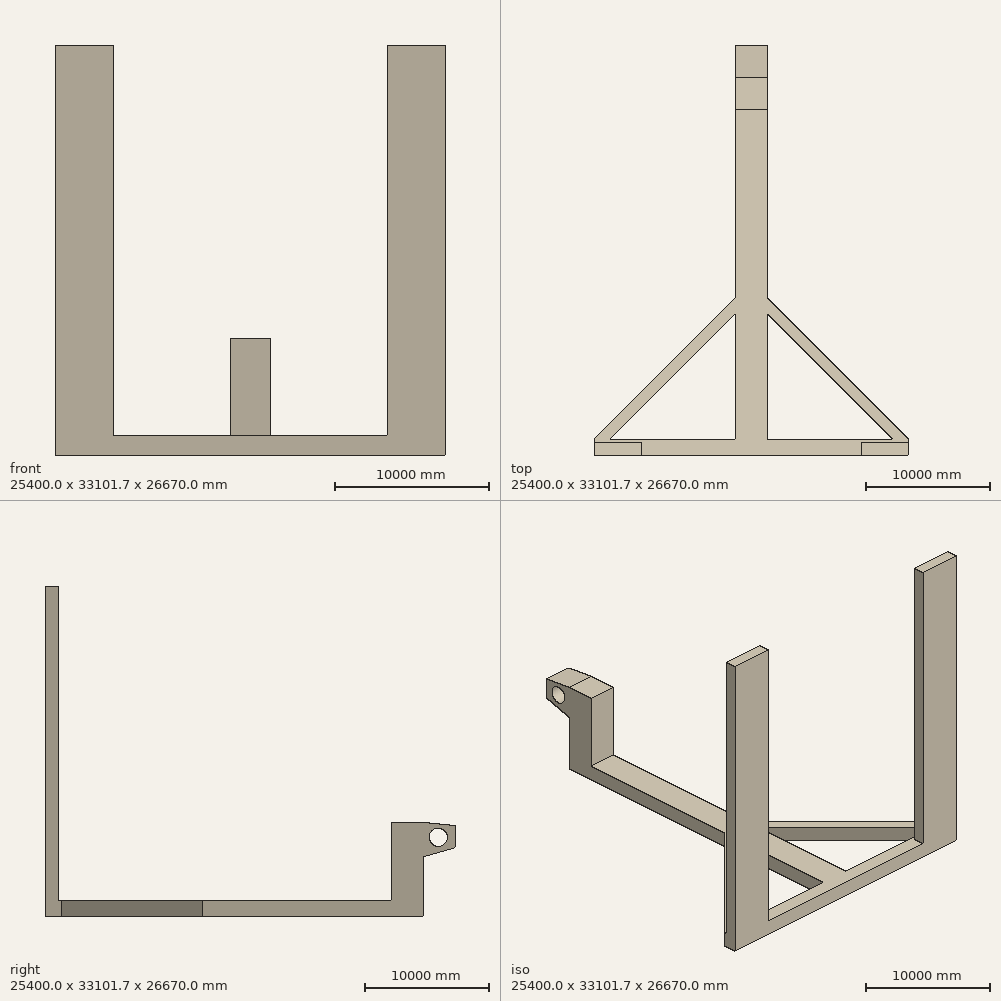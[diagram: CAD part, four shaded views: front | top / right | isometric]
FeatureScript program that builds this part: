
annotation { "Feature Type Name" : "Feature", "Feature Type Description" : "" }
export const myFeature = defineFeature(function(context is Context, id is Id, definition is map)
    precondition{}
    {
        {
            var Q0;
            Q0=qCreatedBy(makeId("Top.planeOp"),FACE);
            var sketch = newSketch(context, id + "F0", { "sketchPlane" : qUnion([Q0])});
            skLineSegment(sketch, "E0", {"start": v(0, 0) * mm, "end": v(28579.32, 0) * mm, "construction": true});
            skLineSegment(sketch, "E1", {"start": v(0, 0) * mm, "end": v(0, 20717.35) * mm, "construction": true});
            skLineSegment(sketch, "E2", {"start": v(0, 0) * mm, "end": v(0, 30480) * mm});
            skLineSegment(sketch, "E3", {"start": v(0, 30480) * mm, "end": v(1270, 30480) * mm});
            skLineSegment(sketch, "E4", {"start": v(1270, 30480) * mm, "end": v(1270, 12700) * mm});
            skLineSegment(sketch, "E5", {"start": v(1270, 12700) * mm, "end": v(12700, 1270) * mm});
            skLineSegment(sketch, "E6", {"start": v(12700, 1270) * mm, "end": v(12700, 0) * mm});
            skLineSegment(sketch, "E7", {"start": v(12700, 0) * mm, "end": v(0, 0) * mm});
            skLineSegment(sketch, "E8", {"start": v(1270, 11430) * mm, "end": v(1270, 1270) * mm});
            skLineSegment(sketch, "E9", {"start": v(1270, 1270) * mm, "end": v(11430, 1270) * mm});
            skLineSegment(sketch, "E10", {"start": v(11430, 1270) * mm, "end": v(1270, 11430) * mm});
            skSolve(sketch);
        }
        {
            var Q0;
            Q0 = qSketchRegion(id + "F0", true);
            extrude(context, id + "F1", {"entities" : qUnion([Q0]), "depth" : 1270 * mm, "offsetDistance" : 25.4 * mm});
        }
        {
            var Q0;
            Q0=makeQuery(id+"F1.opExtrude","CAP_FACE",FACE,{"disambiguationData":[OSD([sQuery(id+"F0.wireOp",EDGE,"E2"),sQuery(id+"F0.wireOp",EDGE,"E3"),sQuery(id+"F0.wireOp",EDGE,"E4"),sQuery(id+"F0.wireOp",EDGE,"E5"),sQuery(id+"F0.wireOp",EDGE,"E6"),sQuery(id+"F0.wireOp",EDGE,"E7"),sQuery(id+"F0.wireOp",EDGE,"E8"),sQuery(id+"F0.wireOp",EDGE,"E9"),sQuery(id+"F0.wireOp",EDGE,"E10")])],"isStart":false});
            var sketch = newSketch(context, id + "F2", { "sketchPlane" : qUnion([Q0])});
            skPoint(sketch, "E11.0", {"position": v(12700, 0) * mm});
            skLineSegment(sketch, "E12.bottom", {"start": v(12700, 0) * mm, "end": v(8890, 0) * mm});
            skLineSegment(sketch, "E12.top", {"start": v(12700, 1016) * mm, "end": v(8890, 1016) * mm});
            skLineSegment(sketch, "E12.left", {"start": v(12700, 0) * mm, "end": v(12700, 1016) * mm});
            skLineSegment(sketch, "E12.right", {"start": v(8890, 0) * mm, "end": v(8890, 1016) * mm});
            skSolve(sketch);
        }
        {
            var Q0;
            Q0 = qSketchRegion(id + "F2", true);
            extrude(context, id + "F3", {"entities" : qUnion([Q0]), "operationType" : NewBodyOperationType.ADD, "depth" : 25400 * mm, "offsetDistance" : 25.4 * mm});
        }
        {
            var Q0;
            Q0=makeQuery(id+"F1.opExtrude","SWEPT_BODY",BODY,{"disambiguationData":[OSD([sQuery(id+"F0.wireOp",EDGE,"E2"),sQuery(id+"F0.wireOp",EDGE,"E3"),sQuery(id+"F0.wireOp",EDGE,"E4"),sQuery(id+"F0.wireOp",EDGE,"E5"),sQuery(id+"F0.wireOp",EDGE,"E6"),sQuery(id+"F0.wireOp",EDGE,"E7"),sQuery(id+"F0.wireOp",EDGE,"E8"),sQuery(id+"F0.wireOp",EDGE,"E9"),sQuery(id+"F0.wireOp",EDGE,"E10")])]});
            var Q1;
            Q1=makeQuery(id+"F1.opExtrude","SWEPT_FACE",FACE,{"disambiguationData":[OSD([sQuery(id+"F0.wireOp",EDGE,"E2")])]});
            mirror(context, id + "F4", {"operationType" : NewBodyOperationType.ADD, "entities" : qUnion([Q0]), "mirrorPlane" : qUnion([Q1])});
        }
        {
            var Q0;
            Q0=makeQuery(id+"F1.opExtrude","SWEPT_FACE",FACE,{"disambiguationData":[OSD([sQuery(id+"F0.wireOp",EDGE,"E4")])]});
            var sketch = newSketch(context, id + "F5", { "sketchPlane" : qUnion([Q0])});
            skPoint(sketch, "E13.0", {"position": v(30480, 0) * mm});
            skLineSegment(sketch, "E14.bottom", {"start": v(30480, 0) * mm, "end": v(27940, 0) * mm});
            skLineSegment(sketch, "E14.top", {"start": v(30480, 7620) * mm, "end": v(27940, 7620) * mm});
            skLineSegment(sketch, "E14.left", {"start": v(30480, 0) * mm, "end": v(30480, 4815.24) * mm});
            skLineSegment(sketch, "E14.right", {"start": v(27940, 0) * mm, "end": v(27940, 7620) * mm});
            skCircle(sketch, "E15", {"center": v(31722.74, 6398.76) * mm, "radius": 735.19 * mm});
            skLineSegment(sketch, "E16", {"start": v(30480, 7620) * mm, "end": v(33101.71, 7350.2) * mm});
            skLineSegment(sketch, "E17", {"start": v(33101.71, 7350.2) * mm, "end": v(33101.71, 5565.02) * mm});
            skLineSegment(sketch, "E18", {"start": v(33101.71, 5565.02) * mm, "end": v(30480, 4815.24) * mm});
            skSolve(sketch);
        }
        {
            var Q0;
            Q0 = qSketchRegion(id + "F5", true);
            extrude(context, id + "F6", {"entities" : qUnion([Q0]), "operationType" : NewBodyOperationType.ADD, "oppositeDirection" : true, "depth" : 2540 * mm, "offsetDistance" : 25.4 * mm});
        }
    });
